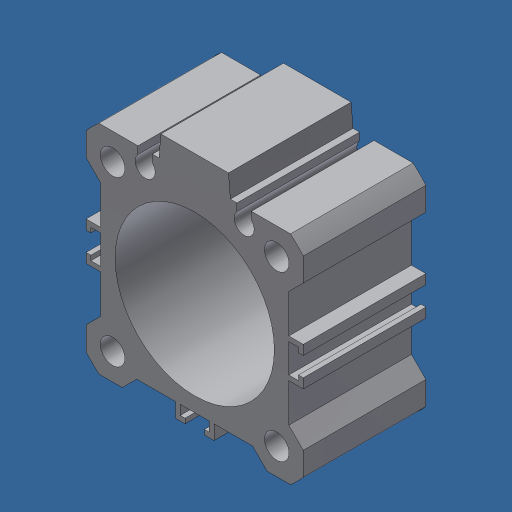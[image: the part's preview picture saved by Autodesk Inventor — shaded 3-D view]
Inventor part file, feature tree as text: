
AUTODESK INVENTOR PART (.ipt)
format: ipt  version: 2024.3 (Build 283343000, 343)  size: 243,200 bytes
history: native  units: mm (DEFAULTED — no unit token found)
features: other x1, extrude x1, hole x1
ambient origin geometry x8: Origin, YZ Plane, XZ Plane, XY Plane, X Axis, Y Axis, Z Axis, Center Point
bodies: Body1 (feature_tree)
feature tree (3):
  other  "Finish - None"
  extrude  "SMC, 32MM"  Depth=33.0mm
  hole  "Hole1"  [1 undecoded]
note: 1 required parameter value undecoded (feature->parameter linkage not recoverable at this tier; creation-order binding heuristic only, values carry confidence <= 0.55)
